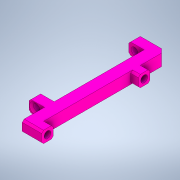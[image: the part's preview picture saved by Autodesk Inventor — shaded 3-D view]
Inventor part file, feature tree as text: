
AUTODESK INVENTOR PART (.ipt)
format: ipt  version: 2020 (Build 240168000, 168)  size: 188,416 bytes
history: native  units: mm
features: chamfer x4, extrude x3, sketch x2
ambient origin geometry x8: Origin, YZ Plane, XZ Plane, XY Plane, X Axis, Y Axis, Z Axis, Center Point
bodies: Solid1 (feature_tree)
feature tree (9):
  extrude  "Extrusion1"  Depth=6.0mm
  extrude  "Extrusion4"  Depth=6.0mm TaperAngle=0.0deg
  chamfer  "Chamfer2"  Distance=6.0mm
  chamfer  "Chamfer3"  Distance=11.5mm
  sketch  "Sketch5"  dims[d4=4.0mm d6=6.0mm d7=0.0mm d19=6.0mm d20=11.5mm d21=5.0mm d22=8.0mm d23=46.5mm d24=3.5mm d25=0.0mm d26=0.0mm d27=1.0mm d28=2.0mm d29=45.0deg d30=2.0mm d31=2.0mm d32=45.0deg d33=3.5mm d34=1.0mm d35=2.0mm d36=45.0deg d37=0.0mm d38=0.0mm d39=1.0mm d40=2.0mm d41=45.0deg]
  chamfer  "Chamfer4"  Distance=5.0mm
  extrude  "Extrusion5"  Depth=8.0mm
  chamfer  "Chamfer5"  Distance=46.5mm
  sketch  "Sketch4"  dims[d2=50.0mm d3=6.0mm]
